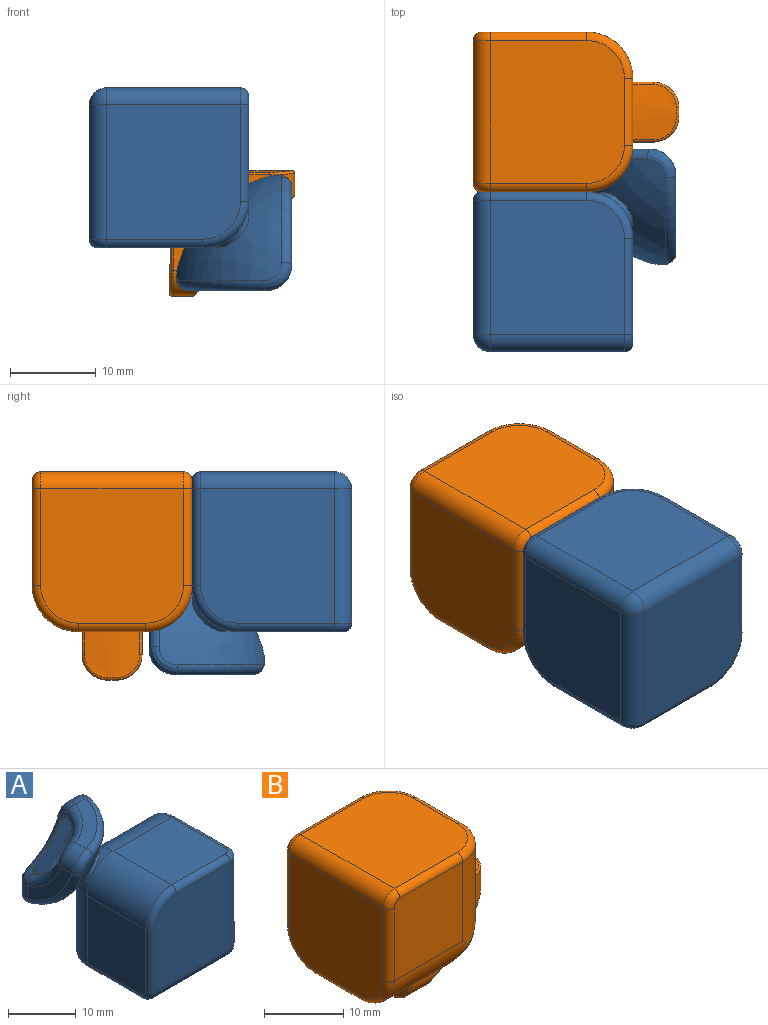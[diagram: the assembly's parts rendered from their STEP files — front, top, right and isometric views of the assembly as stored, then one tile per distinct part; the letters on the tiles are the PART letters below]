
ASSEMBLY  parts=2 mates=1
PART A: 54 faces, bbox 28.2x28.2x24.1 mm
  f0: plane 12.25x12.25mm, normal (-1,0,0), area 149.8mm2, adj f11,f13,f14,f16,f18
  f1: plane 15.65x15.65mm, normal (0,-1,0), area 240.8mm2, adj f2,f9,f18,f20,f22
  f2: cylinder r=2mm len=15.65mm, axis (0,0,1), area 49.2mm2, adj f1,f3,f8,f24
  f3: plane 15.65x15.65mm, normal (1,0,0), area 240.8mm2, adj f2,f7,f21,f23,f25
  f4: plane 12.25x12.25mm, normal (0,1,0), area 149.8mm2, adj f10,f13,f17,f19,f21
  f5: plane 15.65x15.65mm, normal (0,0,-1), area 240.8mm2, adj f7,f9,f14,f15,f17
  f6: plane 12.25x12.25mm, normal (0,0,1), area 149.8mm2, adj f10,f11,f22,f24,f25
  f7: cylinder r=2mm len=15.65mm, axis (0,-1,0), area 49.2mm2, adj f3,f5,f8,f19
  f8: sphere r=2mm, area 6.3mm2, adj f2,f7,f9
  f9: cylinder r=2mm len=15.65mm, axis (-1,0,0), area 49.2mm2, adj f1,f5,f8,f16
  f10: cylinder r=5.4mm len=12.25mm, axis (-1,0,0), area 103.9mm2, adj f4,f6,f12,f23
  f11: cylinder r=5.4mm len=12.25mm, axis (0,-1,0), area 103.9mm2, adj f0,f6,f12,f20
  f12: sphere r=5.4mm, area 15.9mm2, adj f10,f11,f13,f26
  f13: cylinder r=5.4mm len=12.25mm, axis (0,0,-1), area 103.9mm2, adj f0,f4,f12,f15
  f14: cylinder r=1mm len=11.25mm, axis (0,1,0), area 17.7mm2, adj f0,f5,f15,f16
  f15: torus R=4.4mm, axis (0,0,1), area 12.4mm2, adj f5,f13,f14,f17
  f16: torus R=1mm, axis (-1,0,0), area 4mm2, adj f0,f9,f14,f18
  f17: cylinder r=1mm len=11.25mm, axis (1,0,0), area 17.7mm2, adj f4,f5,f15,f19
  f18: cylinder r=1mm len=11.25mm, axis (0,0,1), area 17.7mm2, adj f0,f1,f16,f20
  f19: torus R=1mm, axis (0,-1,0), area 4mm2, adj f4,f7,f17,f21
  f20: torus R=4.4mm, axis (0,-1,0), area 12.4mm2, adj f1,f11,f18,f22
  f21: cylinder r=1mm len=11.25mm, axis (0,0,1), area 17.7mm2, adj f3,f4,f19,f23
  f22: cylinder r=1mm len=11.25mm, axis (1,0,0), area 17.7mm2, adj f1,f6,f20,f24
  f23: torus R=4.4mm, axis (-1,0,0), area 12.4mm2, adj f3,f10,f21,f25
  f24: torus R=1mm, axis (0,0,1), area 4mm2, adj f2,f6,f22,f25
  f25: cylinder r=1mm len=11.25mm, axis (0,1,0), area 17.7mm2, adj f3,f6,f23,f24
  f26: cylinder r=2.96mm len=5.2mm, axis (0.58,-0.58,-0.58), area 11.9mm2, adj f12,f29
  f27: sphere r=10.75mm, area 11.9mm2, adj f41,f42,f43,f44,f45,f46,f47,f49
  f28: plane 9.22x9.22mm, normal (-1,0,0), area 25.3mm2, adj f32,f34,f35,f45
  f29: sphere r=15.25mm, area 181.2mm2, adj f26,f35,f36,f37,f38,f39,f40
  f30: plane 9.22x9.22mm, normal (0,1,0), area 25.3mm2, adj f33,f34,f38,f44
  f31: plane 9.22x9.22mm, normal (0,0,1), area 25.3mm2, adj f32,f33,f39,f41
  f32: cylinder r=3mm len=3mm, axis (0,1,0), area 10.7mm2, adj f28,f31,f37,f43
  f33: cylinder r=3mm len=3mm, axis (1,0,0), area 10.7mm2, adj f30,f31,f40,f42
  f34: cylinder r=3mm len=3mm, axis (0,0,-1), area 10.7mm2, adj f28,f30,f36,f46
  f35: torus R=14.08mm, axis (-1,0,0), area 24.5mm2, adj f28,f29,f36,f37
  f36: bspline ~4.11x4.11mm, area 8mm2, adj f29,f34,f35,f38
  f37: bspline ~4.11x4.11mm, area 8mm2, adj f29,f32,f35,f39
  f38: torus R=14.08mm, axis (0,1,0), area 24.5mm2, adj f29,f30,f36,f40
  f39: torus R=14.08mm, axis (0,0,1), area 24.5mm2, adj f29,f31,f37,f40
  f40: bspline ~4.11x4.11mm, area 8mm2, adj f29,f33,f38,f39
  f41: torus R=11.95mm, axis (0,0,1), area 19mm2, adj f27,f31,f42,f43
  f42: bspline ~3.76x3.76mm, area 6.7mm2, adj f27,f33,f41,f44
  f43: bspline ~3.76x3.76mm, area 6.7mm2, adj f27,f32,f41,f45
  f44: torus R=11.95mm, axis (0,1,0), area 19mm2, adj f27,f30,f42,f46
  f45: torus R=11.95mm, axis (-1,0,0), area 19mm2, adj f27,f28,f43,f46
  f46: bspline ~3.76x3.76mm, area 6.7mm2, adj f27,f34,f44,f45
  f47: plane 8.59x8.59mm, normal (1,0,0), area 31.2mm2, adj f27,f48,f51,f53
  f48: sphere r=13.75mm, area 141.9mm2, adj f47,f49,f50,f51,f52,f53
  f49: plane 8.59x8.59mm, normal (0,-1,0), area 31.2mm2, adj f27,f48,f52,f53
  f50: plane 8.59x8.59mm, normal (0,0,-1), area 31.2mm2, adj f27,f48,f51,f52
  f51: cylinder r=1.5mm len=3.5mm, axis (0,1,0), area 7.7mm2, adj f27,f47,f48,f50
  f52: cylinder r=1.5mm len=3.5mm, axis (1,0,0), area 7.7mm2, adj f27,f48,f49,f50
  f53: cylinder r=1.5mm len=3.5mm, axis (0,0,-1), area 7.7mm2, adj f27,f47,f48,f49
PART B: 58 faces, bbox 25.5x20.8x25.7 mm
  f0: plane 10.69x7.85mm, normal (1,0,0), area 70.2mm2, adj f4,f12,f14,f18,f30,f36,f37,f40
  f1: plane 10.4x7.85mm, normal (0,0,-1), area 68mm2, adj f3,f11,f13,f23,f29,f33,f34,f35
  f2: cylinder r=18.62mm len=6.51mm, axis (0,1,0), area 36.1mm2, adj f3,f4,f31,f32,f37
  f3: cylinder r=0.55mm len=0.47mm, axis (0,1,0), area 0.2mm2, adj f1,f2,f31,f37
  f4: cylinder r=0.55mm len=0.48mm, axis (0,1,0), area 0.2mm2, adj f0,f2,f32,f37
  f5: plane 12.25x12.25mm, normal (0,1,0), area 149.8mm2, adj f11,f12,f22,f24,f26
  f6: plane 16.65x15.65mm, normal (0,0,1), area 252.3mm2, adj f7,f15,f16,f18,f20,f22
  f7: cylinder r=2mm len=16.65mm, axis (0,1,0), area 52.3mm2, adj f6,f8,f17,f24
  f8: plane 16.65x15.65mm, normal (-1,0,0), area 252.3mm2, adj f7,f19,f21,f23,f25,f26
  f9: plane 12.25x12.25mm, normal (0,-1,0), area 149.8mm2, adj f13,f14,f15,f17,f19
  f10: cylinder r=18.62mm len=6.51mm, axis (0,1,0), area 36.1mm2, adj f27,f28,f29,f30,f36
  f11: cylinder r=5.4mm len=13.49mm, axis (1,0,0), area 98.5mm2, adj f1,f5,f12,f25,f27,f28
  f12: cylinder r=5.4mm len=13.49mm, axis (0,0,1), area 103.5mm2, adj f0,f5,f11,f20,f28
  f13: cylinder r=5.4mm len=13.49mm, axis (-1,0,0), area 98.5mm2, adj f1,f9,f14,f21,f31,f32
  f14: cylinder r=5.4mm len=13.49mm, axis (0,0,-1), area 103.5mm2, adj f0,f9,f13,f16,f32
  f15: cylinder r=1mm len=11.25mm, axis (1,0,0), area 17.7mm2, adj f6,f9,f16,f17
  f16: torus R=4.4mm, axis (0,0,1), area 12.4mm2, adj f6,f14,f15,f18
  f17: torus R=1mm, axis (0,-1,0), area 4mm2, adj f7,f9,f15,f19
  f18: cylinder r=1mm len=7.85mm, axis (0,1,0), area 12.3mm2, adj f0,f6,f16,f20
  f19: cylinder r=1mm len=11.25mm, axis (0,0,1), area 17.7mm2, adj f8,f9,f17,f21
  f20: torus R=4.4mm, axis (0,0,1), area 12.4mm2, adj f6,f12,f18,f22
  f21: torus R=4.4mm, axis (1,0,0), area 12.4mm2, adj f8,f13,f19,f23
  f22: cylinder r=1mm len=11.25mm, axis (-1,0,0), area 17.7mm2, adj f5,f6,f20,f24
  f23: cylinder r=1mm len=7.85mm, axis (0,1,0), area 12.3mm2, adj f1,f8,f21,f25
  f24: torus R=1mm, axis (0,-1,0), area 4mm2, adj f5,f7,f22,f26
  f25: torus R=4.4mm, axis (1,0,0), area 12.4mm2, adj f8,f11,f23,f26
  f26: cylinder r=1mm len=11.25mm, axis (0,0,-1), area 17.7mm2, adj f5,f8,f24,f25
  f27: bspline ~6.4x4.72mm, area 4.8mm2, adj f10,f11,f28,f29
  f28: bspline ~6.4x4.54mm, area 4.8mm2, adj f10,f11,f12,f27,f30
  f29: cylinder r=0.55mm len=0.47mm, axis (0,1,0), area 0.2mm2, adj f1,f10,f27,f36
  f30: cylinder r=0.55mm len=0.48mm, axis (0,1,0), area 0.2mm2, adj f0,f10,f28,f36
  f31: bspline ~6.4x4.72mm, area 4.8mm2, adj f2,f3,f13,f32
  f32: bspline ~6.4x4.54mm, area 4.8mm2, adj f2,f4,f13,f14,f31
  f33: cylinder r=27.65mm len=6.47mm, axis (0,0,-1), area 31.5mm2, adj f1,f34,f35,f52,f54,f56
  f34: cylinder r=0.3mm len=2.65mm, axis (0,0,-1), area 1.2mm2, adj f1,f33,f37,f52
  f35: cylinder r=0.3mm len=2.65mm, axis (0,0,-1), area 1.2mm2, adj f1,f33,f36,f56
  f36: plane 11.26x11.16mm, normal (0,1,0), area 64.9mm2, adj f0,f1,f10,f29,f30,f35,f39,f42
  f37: plane 11.26x11.16mm, normal (0,-1,0), area 64.9mm2, adj f0,f1,f2,f3,f4,f34,f38,f41
  f38: cylinder r=3mm len=5.53mm, axis (-1,0,0), area 18.5mm2, adj f37,f45,f46,f52
  f39: cylinder r=3mm len=5.53mm, axis (1,0,0), area 18.5mm2, adj f36,f45,f46,f56
  f40: cylinder r=27.65mm len=6.47mm, axis (1,0,0), area 29.7mm2, adj f0,f50,f51,f53,f55,f57
  f41: cylinder r=3mm len=5.61mm, axis (0,0,1), area 19mm2, adj f37,f43,f44,f51
  f42: cylinder r=3mm len=5.61mm, axis (0,0,1), area 19mm2, adj f36,f43,f44,f55
  f43: plane 8.25x4.64mm, normal (0.7,0,-0.71), area 28mm2, adj f36,f37,f41,f42,f44,f48
  f44: plane 2.65x1mm, normal (1,0,0), area 2.6mm2, adj f41,f42,f43,f53
  f45: plane 2.5x1mm, normal (0,0,-1), area 2.5mm2, adj f38,f39,f46,f54
  f46: plane 8.28x4.96mm, normal (0.7,0,-0.71), area 30.8mm2, adj f36,f37,f38,f39,f45,f47
  f47: plane 7x0.5mm, normal (-0.71,0,-0.7), area 4.9mm2, adj f36,f37,f46,f49
  f48: plane 7x0.5mm, normal (0.71,0,0.7), area 4.9mm2, adj f36,f37,f43,f49
  f49: plane 7x4.77mm, normal (0.7,0,-0.71), area 46.9mm2, adj f36,f37,f47,f48
  f50: cylinder r=0.3mm len=2.37mm, axis (1,0,0), area 1mm2, adj f0,f37,f40,f51
  f51: bspline ~3.67x3.17mm, area 2.1mm2, adj f40,f41,f50,f53
  f52: bspline ~3.67x3.67mm, area 2.1mm2, adj f33,f34,f38,f54
  f53: torus R=27.35mm, axis (1,0,0), area 0.5mm2, adj f40,f44,f51,f55
  f54: torus R=27.35mm, axis (0,0,1), area 0.5mm2, adj f33,f45,f52,f56
  f55: bspline ~3.67x3.17mm, area 2.1mm2, adj f40,f42,f53,f57
  f56: bspline ~3.67x3.17mm, area 2.1mm2, adj f33,f35,f39,f54
  f57: cylinder r=0.3mm len=2.37mm, axis (1,0,0), area 1mm2, adj f0,f36,f40,f55
PLACE A rot(axis=(0,1,0),180deg) t=(77.98,5.58,15.59)mm
PLACE B at identity
MATE planar A.f4 <-> B.f9  axis (0,1,0) through (32,-18.65,27.11)mm
